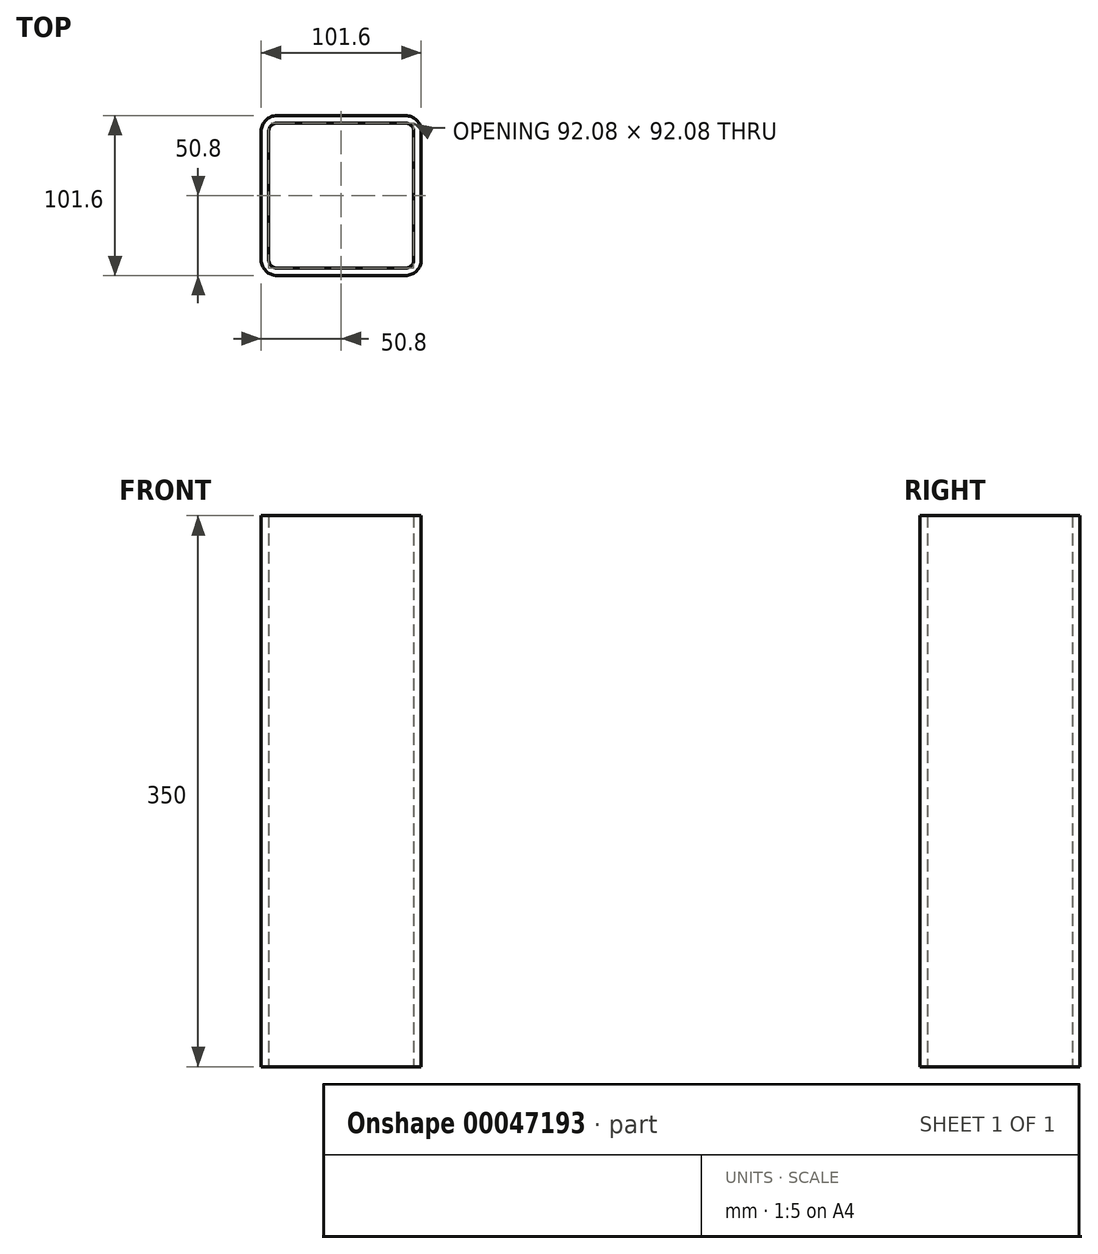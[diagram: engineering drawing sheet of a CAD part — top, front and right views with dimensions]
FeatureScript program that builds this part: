
annotation { "Feature Type Name" : "Feature", "Feature Type Description" : "" }
export const myFeature = defineFeature(function(context is Context, id is Id, definition is map)
    precondition{}
    {
        {
            var Q0;
            Q0=qCreatedBy(makeId("Top.planeOp"),FACE);
            var sketch = newSketch(context, id + "F0", { "sketchPlane" : qUnion([Q0])});
            skLineSegment(sketch, "E0.bottom", {"start": v(-40.8, 50.8) * mm, "end": v(40.8, 50.8) * mm});
            skLineSegment(sketch, "E0.top", {"start": v(-40.8, -50.8) * mm, "end": v(40.8, -50.8) * mm});
            skLineSegment(sketch, "E0.left", {"start": v(-50.8, 40.8) * mm, "end": v(-50.8, -40.8) * mm});
            skLineSegment(sketch, "E0.right", {"start": v(50.8, 40.8) * mm, "end": v(50.8, -40.8) * mm});
            skLineSegment(sketch, "E1", {"start": v(-50.8, 0) * mm, "end": v(50.8, 0) * mm, "construction": true});
            skPoint(sketch, "E2.visualSharp", {"position": v(-50.8, 50.8) * mm});
            skArc(sketch, "E2.filletArc", {"start": v(-40.8, 50.8) * mm, "mid": v(-47.87, 47.87) * mm, "end": v(-50.8, 40.8) * mm});
            skPoint(sketch, "E3.visualSharp", {"position": v(-50.8, -50.8) * mm});
            skArc(sketch, "E3.filletArc", {"start": v(-50.8, -40.8) * mm, "mid": v(-47.87, -47.87) * mm, "end": v(-40.8, -50.8) * mm});
            skPoint(sketch, "E4.visualSharp", {"position": v(50.8, -50.8) * mm});
            skArc(sketch, "E4.filletArc", {"start": v(40.8, -50.8) * mm, "mid": v(47.87, -47.87) * mm, "end": v(50.8, -40.8) * mm});
            skPoint(sketch, "E5.visualSharp", {"position": v(50.8, 50.8) * mm});
            skArc(sketch, "E5.filletArc", {"start": v(50.8, 40.8) * mm, "mid": v(47.87, 47.87) * mm, "end": v(40.8, 50.8) * mm});
            skLineSegment(sketch, "E6.0", {"start": v(-40.8, 46.04) * mm, "end": v(40.8, 46.04) * mm});
            skArc(sketch, "E6.1", {"start": v(46.04, 40.8) * mm, "mid": v(44.5, 44.5) * mm, "end": v(40.8, 46.04) * mm});
            skArc(sketch, "E6.2", {"start": v(-40.8, 46.04) * mm, "mid": v(-44.5, 44.5) * mm, "end": v(-46.04, 40.8) * mm});
            skLineSegment(sketch, "E6.3", {"start": v(46.04, 40.8) * mm, "end": v(46.04, -40.8) * mm});
            skLineSegment(sketch, "E6.4", {"start": v(-46.04, 40.8) * mm, "end": v(-46.04, -40.8) * mm});
            skArc(sketch, "E6.5", {"start": v(-46.04, -40.8) * mm, "mid": v(-44.5, -44.5) * mm, "end": v(-40.8, -46.04) * mm});
            skLineSegment(sketch, "E6.6", {"start": v(-40.8, -46.04) * mm, "end": v(40.8, -46.04) * mm});
            skArc(sketch, "E6.7", {"start": v(40.8, -46.04) * mm, "mid": v(44.5, -44.5) * mm, "end": v(46.04, -40.8) * mm});
            skSolve(sketch);
        }
        {
            var Q0;
            Q0 = qSketchRegion(id + "F0", true);
            extrude(context, id + "F1", {"entities" : qUnion([Q0]), "endBound" : BoundingType.SYMMETRIC, "depth" : 350 * mm});
        }
    });
